# Revit family: LeL Reiko 1.0
name_source: partatom
category: Lighting Fixtures
units: mm (PartAtom-declared; Revit-internal decimal feet)

## family parameters
Always vertical = No
Cut with Voids When Loaded = No
Light Source = No
OmniClass Number = 23.80.70.00
OmniClass Title = Lighting
Part Type = Normal
Room Calculation Point = No
Round Connector Dimension = Use Diameter
Shared = No
Work Plane-Based = Yes

## types (14) — shared parameters
CCT = 3000 K
CRI = CRI80
Default Elevation = 1219 mm
Description = Outdoor Projectors
IK = IK06
IP = IP66
Lamp = LED
Manufacturer = L&L Luce&Light srl
Model = RK10
Rated Power supply = 24 V
URL = https://www.lucelight.it
Weight = 0.25 kg

## per-type parameters (varying)
| type | Apparent Load | Lumen Output | Photometry | Wattage |
| X 34°x18° 2.5W | 3 VA | 129 lm | RK10 Light source : X 34°x18° 2.5W | 3 W |
| W 18°x34° 2.5W | 3 VA | 129 lm | RK10 Light source : W 18°x34° 2.5W | 3 W |
| K 59° 2.5W | 3 VA | 95 lm | RK10 Light source : K 59° 2.5W | 3 W |
| K 59° 3.5W | 4 VA | 134 lm | RK10 Light source : K 59° 3.5W | 4 W |
| L 38° 2.5W | 3 VA | 109 lm | RK10 Light source : L 38° 2.5W | 3 W |
| L 38° 3.5W | 4 VA | 154 lm | RK10 Light source : L 38° 3.5W | 4 W |
| M 21° 2.5W | 3 VA | 129 lm | RK10 Light source : M 21° 2.5W | 3 W |
| M 21° 3.5W | 4 VA | 182 lm | RK10 Light source : M 21° 3.5W | 4 W |
| P (38°) 2.5W | 3 VA | 35 lm | RK10 Light source : P (38°) 2.5W | 3 W |
| P (38°) 3.5W | 4 VA | 50 lm | RK10 Light source : P (38°) 3.5W | 4 W |
| S 17° 2.5W | 3 VA | 113 lm | RK10 Light source : S 17° 2.5W | 3 W |
| S 17° 3.5W | 4 VA | 159 lm | RK10 Light source : S 17° 3.5W | 4 W |
| W 18°x34° 3.5W | 4 VA | 181 lm | RK10 Light source : W 18°x34° 3.5W | 4 W |
| X 34°x18° 3.5W | 4 VA | 181 lm | RK10 Light source : X 34°x18° 3.5W | 4 W |

## geometry (parser evidence)
native form markers: Sweep x1
no freeform markers — native parametric forms only
